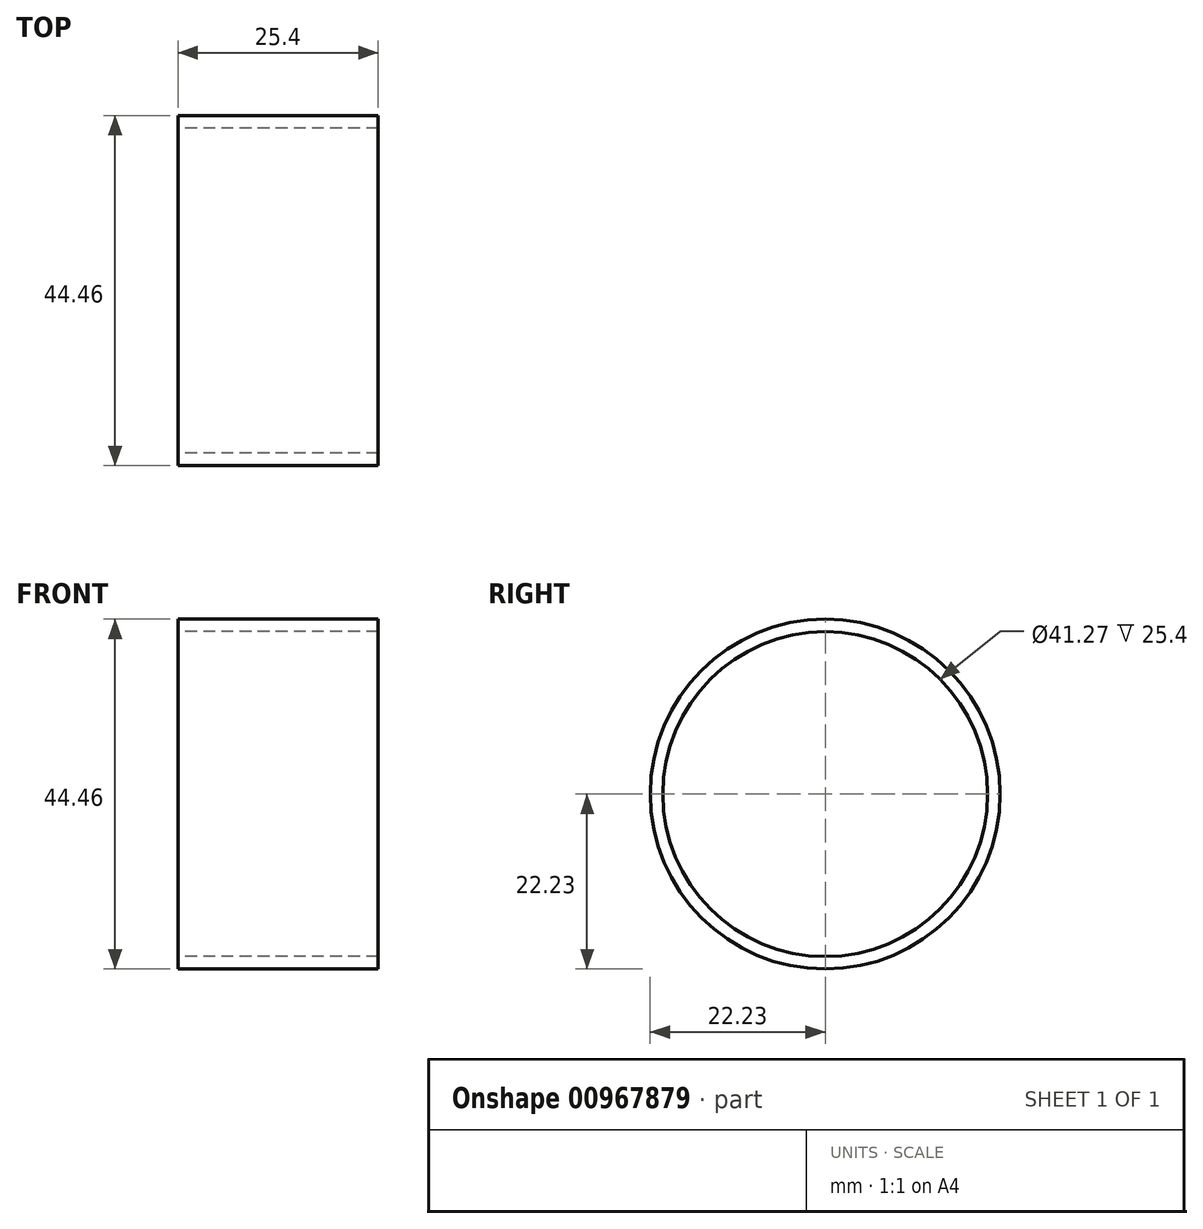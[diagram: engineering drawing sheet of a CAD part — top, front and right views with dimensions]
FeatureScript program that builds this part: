
annotation { "Feature Type Name" : "Feature", "Feature Type Description" : "" }
export const myFeature = defineFeature(function(context is Context, id is Id, definition is map)
    precondition{}
    {
        {
            var Q0;
            Q0=qCreatedBy(makeId("Right.planeOp"),FACE);
            var sketch = newSketch(context, id + "F0", { "sketchPlane" : qUnion([Q0])});
            skCircle(sketch, "E0", {"center": v(0, 0) * mm, "radius": 22.23 * mm});
            skCircle(sketch, "E1", {"center": v(0, 0) * mm, "radius": 20.64 * mm});
            skPoint(sketch, "E2", {"position": v(0, 20.64) * mm});
            skPoint(sketch, "E3", {"position": v(0, 22.23) * mm});
            skSolve(sketch);
        }
        {
            var Q0;
            Q0=makeQuery(id+"F0.imprint","IMPRINT",FACE,{"disambiguationData":[TD([[makeQuery(id+"F0.imprint","IMPRINT",EDGE,{"derivedFrom":sQuery(id+"F0.wireOp",EDGE,"E0")}),1.0]])]});
            extrude(context, id + "F1", {"entities" : qUnion([Q0]), "endBound" : BoundingType.SYMMETRIC, "depth" : 25.4 * mm, "offsetDistance" : 25.4 * mm});
        }
    });
